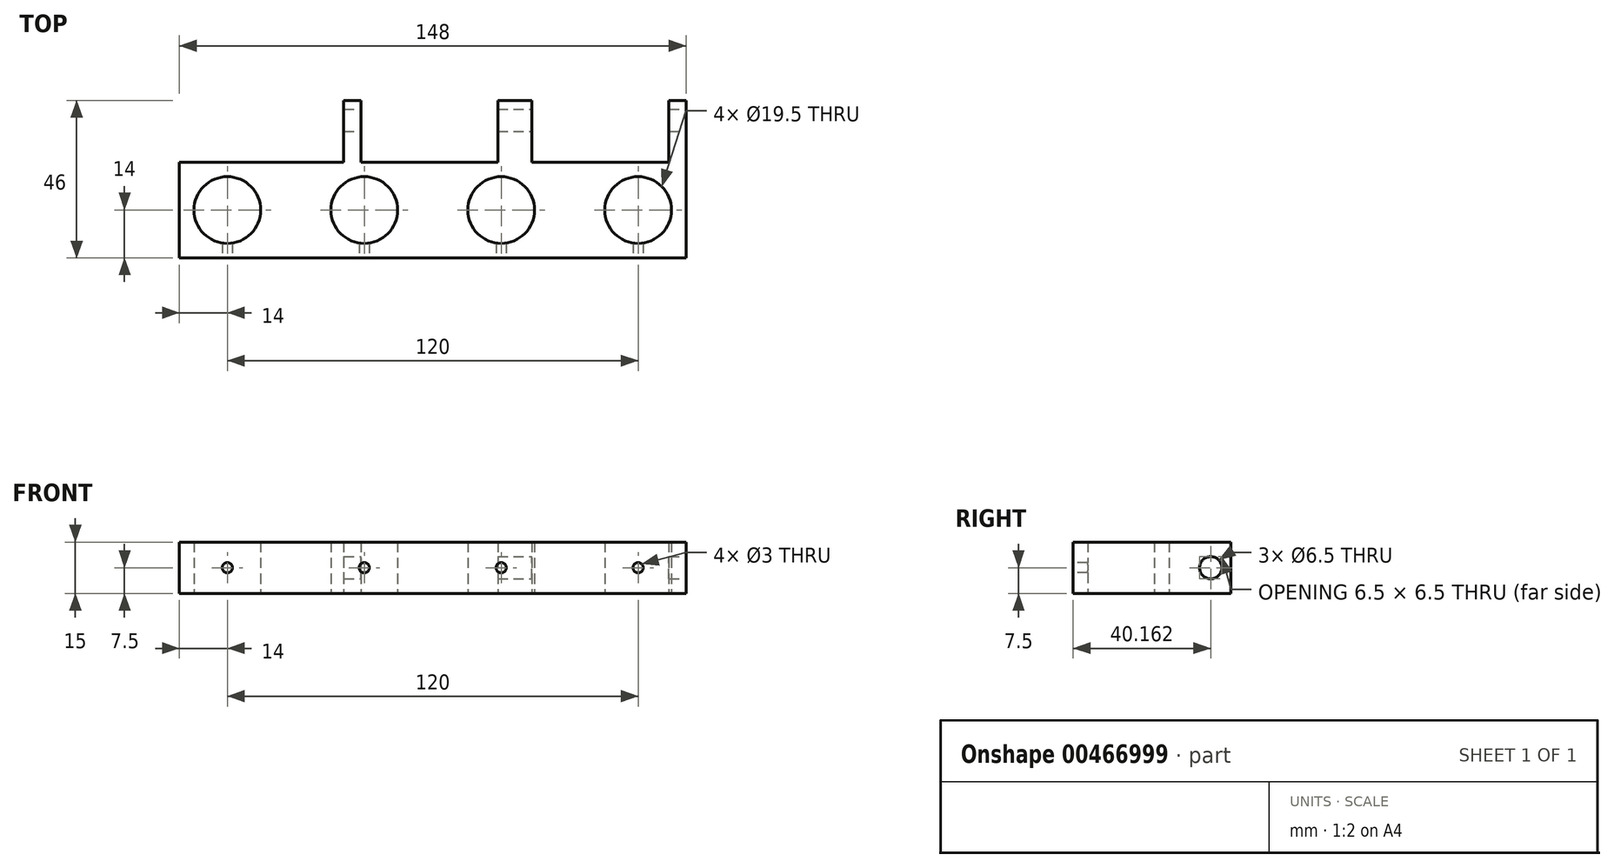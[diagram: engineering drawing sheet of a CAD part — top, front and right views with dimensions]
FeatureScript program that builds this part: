
annotation { "Feature Type Name" : "Feature", "Feature Type Description" : "" }
export const myFeature = defineFeature(function(context is Context, id is Id, definition is map)
    precondition{}
    {
        {
            var Q0;
            Q0=qCreatedBy(makeId("Top.planeOp"),FACE);
            var sketch = newSketch(context, id + "F0", { "sketchPlane" : qUnion([Q0])});
            skLineSegment(sketch, "E0", {"start": v(0, 0) * mm, "end": v(40, 0) * mm, "construction": true});
            skLineSegment(sketch, "E1", {"start": v(40, 0) * mm, "end": v(80, 0) * mm, "construction": true});
            skLineSegment(sketch, "E2", {"start": v(80, 0) * mm, "end": v(120, 0) * mm, "construction": true});
            skCircle(sketch, "E3", {"center": v(0, 0) * mm, "radius": 9.75 * mm});
            skCircle(sketch, "E4", {"center": v(40, 0) * mm, "radius": 9.75 * mm});
            skCircle(sketch, "E5", {"center": v(80, 0) * mm, "radius": 9.75 * mm});
            skCircle(sketch, "E6", {"center": v(120, 0) * mm, "radius": 9.75 * mm});
            skLineSegment(sketch, "E7", {"start": v(0, 0) * mm, "end": v(-14, 0) * mm, "construction": true});
            skLineSegment(sketch, "E8", {"start": v(-14, 0) * mm, "end": v(-14, 14) * mm, "construction": true});
            skLineSegment(sketch, "E9.bottom", {"start": v(-14, 14) * mm, "end": v(34, 14) * mm});
            skLineSegment(sketch, "E9.top", {"start": v(-14, -14) * mm, "end": v(134, -14) * mm});
            skLineSegment(sketch, "E9.left", {"start": v(-14, 14) * mm, "end": v(-14, -14) * mm});
            skLineSegment(sketch, "E9.right", {"start": v(134, 14) * mm, "end": v(134, -14) * mm});
            skLineSegment(sketch, "E10", {"start": v(134, 14) * mm, "end": v(134, 32) * mm});
            skLineSegment(sketch, "E11", {"start": v(134, 32) * mm, "end": v(129, 32) * mm});
            skLineSegment(sketch, "E12", {"start": v(129, 32) * mm, "end": v(129, 14) * mm});
            skLineSegment(sketch, "E13", {"start": v(129, 14) * mm, "end": v(89, 14) * mm, "construction": true});
            skLineSegment(sketch, "E14", {"start": v(34, 14) * mm, "end": v(34, 32) * mm});
            skLineSegment(sketch, "E15", {"start": v(34, 32) * mm, "end": v(39, 32) * mm});
            skLineSegment(sketch, "E16", {"start": v(39, 32) * mm, "end": v(39, 14) * mm});
            skLineSegment(sketch, "E17", {"start": v(39, 14) * mm, "end": v(79, 14) * mm});
            skLineSegment(sketch, "E18", {"start": v(79, 14) * mm, "end": v(79, 32) * mm});
            skLineSegment(sketch, "E19", {"start": v(79, 32) * mm, "end": v(89, 32) * mm});
            skLineSegment(sketch, "E20", {"start": v(89, 32) * mm, "end": v(89, 14) * mm});
            skLineSegment(sketch, "E21.trimOffspring", {"start": v(79, 14) * mm, "end": v(39, 14) * mm, "construction": true});
            skLineSegment(sketch, "E22.trimOffspring", {"start": v(89, 14) * mm, "end": v(129, 14) * mm});
            skSolve(sketch);
        }
        {
            var Q0;
            Q0=makeQuery(id+"F0.imprint","IMPRINT",FACE,{"disambiguationData":[TD([[makeQuery(id+"F0.imprint","IMPRINT",EDGE,{"derivedFrom":sQuery(id+"F0.wireOp",EDGE,"E3")}),-1.0]])]});
            extrude(context, id + "F1", {"entities" : qUnion([Q0]), "depth" : 15 * mm});
        }
        {
            var Q0;
            Q0=makeQuery(id+"F1.opExtrude","SWEPT_FACE",FACE,{"disambiguationData":[OSD([sQuery(id+"F0.wireOp",EDGE,"E9.right"),sQuery(id+"F0.wireOp",EDGE,"E10")])]});
            var sketch = newSketch(context, id + "F2", { "sketchPlane" : qUnion([Q0])});
            skLineSegment(sketch, "E23", {"start": v(32, 7.5) * mm, "end": v(-14, 7.5) * mm, "construction": true});
            skCircle(sketch, "E24", {"center": v(26.16, 7.5) * mm, "radius": 3.25 * mm});
            skSolve(sketch);
        }
        {
            var Q0;
            Q0=makeQuery(id+"F2.imprint","IMPRINT",FACE,{"disambiguationData":[TD([[makeQuery(id+"F2.imprint","IMPRINT",EDGE,{"derivedFrom":sQuery(id+"F2.wireOp",EDGE,"E24")}),1.0]])]});
            extrude(context, id + "F3", {"entities" : qUnion([Q0]), "operationType" : NewBodyOperationType.REMOVE, "oppositeDirection" : true, "depth" : 125 * mm});
        }
        {
            var Q0;
            Q0=makeQuery(id+"F1.opExtrude","SWEPT_FACE",FACE,{"disambiguationData":[OSD([sQuery(id+"F0.wireOp",EDGE,"E9.top")])]});
            var sketch = newSketch(context, id + "F4", { "sketchPlane" : qUnion([Q0])});
            skLineSegment(sketch, "E25", {"start": v(134, 7.5) * mm, "end": v(-14, 7.5) * mm, "construction": true});
            skLineSegment(sketch, "E26", {"start": v(60, 7.5) * mm, "end": v(40, 7.5) * mm, "construction": true});
            skLineSegment(sketch, "E27", {"start": v(40, 7.5) * mm, "end": v(0, 7.5) * mm, "construction": true});
            skLineSegment(sketch, "E28", {"start": v(60, 7.5) * mm, "end": v(80, 7.5) * mm, "construction": true});
            skLineSegment(sketch, "E29", {"start": v(80, 7.5) * mm, "end": v(120, 7.5) * mm, "construction": true});
            skCircle(sketch, "E30", {"center": v(120, 7.5) * mm, "radius": 1.5 * mm});
            skCircle(sketch, "E31", {"center": v(80, 7.5) * mm, "radius": 1.5 * mm});
            skCircle(sketch, "E32", {"center": v(40, 7.5) * mm, "radius": 1.5 * mm});
            skCircle(sketch, "E33", {"center": v(0, 7.5) * mm, "radius": 1.5 * mm});
            skSolve(sketch);
        }
        {
            var Q0;
            Q0=makeQuery(id+"F4.imprint","IMPRINT",FACE,{"disambiguationData":[TD([[makeQuery(id+"F4.imprint","IMPRINT",EDGE,{"derivedFrom":sQuery(id+"F4.wireOp",EDGE,"E30")}),1.0]])]});
            var Q1;
            Q1=makeQuery(id+"F4.imprint","IMPRINT",FACE,{"disambiguationData":[TD([[makeQuery(id+"F4.imprint","IMPRINT",EDGE,{"derivedFrom":sQuery(id+"F4.wireOp",EDGE,"E31")}),1.0]])]});
            var Q2;
            Q2=makeQuery(id+"F4.imprint","IMPRINT",FACE,{"disambiguationData":[TD([[makeQuery(id+"F4.imprint","IMPRINT",EDGE,{"derivedFrom":sQuery(id+"F4.wireOp",EDGE,"E32")}),1.0]])]});
            var Q3;
            Q3=makeQuery(id+"F4.imprint","IMPRINT",FACE,{"disambiguationData":[TD([[makeQuery(id+"F4.imprint","IMPRINT",EDGE,{"derivedFrom":sQuery(id+"F4.wireOp",EDGE,"E33")}),1.0]])]});
            var Q4;
            Q4=sQuery(id+"F4.wireOp",EDGE,"E30");
            var Q5;
            Q5=sQuery(id+"F4.wireOp",EDGE,"E31");
            var Q6;
            Q6=sQuery(id+"F4.wireOp",EDGE,"E32");
            var Q7;
            Q7=sQuery(id+"F4.wireOp",EDGE,"E33");
            extrude(context, id + "F5", {"entities" : qUnion([Q0, Q1, Q2, Q3]), "operationType" : NewBodyOperationType.REMOVE, "surfaceEntities" : qUnion([Q4, Q5, Q6, Q7]), "oppositeDirection" : true, "depth" : 8 * mm});
        }
    });
